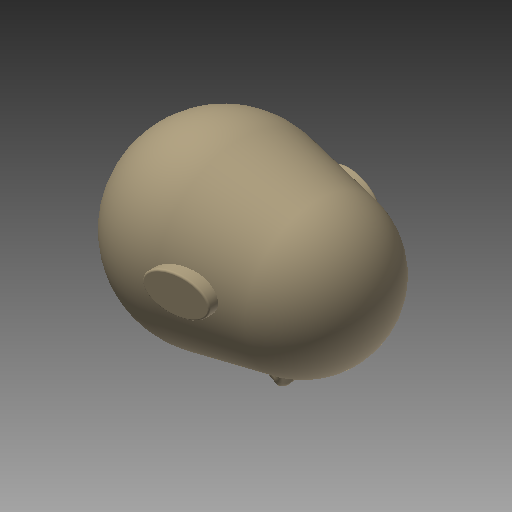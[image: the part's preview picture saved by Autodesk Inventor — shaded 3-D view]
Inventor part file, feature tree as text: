
AUTODESK INVENTOR PART (.ipt)
format: ipt  version: 2022 (Build 260153000, 153)  size: 293,376 bytes
history: native  units: mm (DEFAULTED — no unit token found)
features: sketch x5, extrude x3, revolve x2, fillet x2, other x1, mirror x1, projected_geometry x1
ambient origin geometry x8: Origin, YZ Plane, XZ Plane, XY Plane, X Axis, Y Axis, Z Axis, Center Point
bodies: Solid1 (feature_tree)
feature tree (15):
  other  "iMandy - 2D BODY"
  revolve  "Revolution1"  [1 undecoded]
  extrude  "Extrusion1"  Depth=153.293747mm
  extrude  "Extrusion2"  Depth=24.479788mm
  mirror  "Mirror1"
  fillet  "Fillet1"  Radius=19.277833mm
  revolve  "Revolution2"  [1 undecoded]
  extrude  "Extrusion3"  Depth=3.693825mm
  fillet  "Fillet2"  [1 undecoded]
  sketch  "Sketch2"  dims[d1=10.0mm d25=250.39193mm]
  sketch  "Sketch3"  dims[d26=184.691261mm d27=153.293747mm]
  projected_geometry  "Projected Loop1"
  sketch  "Sketch4"  dims[d28=90.0deg d29=24.479788mm d30=19.277833mm]
  sketch  "Sketch5"  dims[d31=30.599736mm d32=193.925824mm]
  sketch  "Sketch6"  dims[d33=0.0mm d34=193.925824mm d35=0.0mm d36=1.846913mm d37=30.0deg d38=180.0deg d39=193.925824mm d40=0.0mm d41=3.693825mm d42=50.078386mm d43=8.89mm]
note: 3 required parameter values undecoded (feature->parameter linkage not recoverable at this tier; creation-order binding heuristic only, values carry confidence <= 0.55)